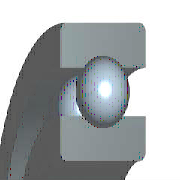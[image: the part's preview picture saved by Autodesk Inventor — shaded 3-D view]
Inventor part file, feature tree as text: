
AUTODESK INVENTOR PART (.ipt)
format: ipt  version: 2021 (Build 250183000, 183)  size: 447,488 bytes
history: native  units: mm (DEFAULTED — no unit token found)
features: sketch x5, other x3, plane x2, pattern_circular x1, fillet x1
ambient origin geometry x8: Origin, YZ Plane, XZ Plane, XY Plane, X Axis, Y Axis, Z Axis, Center Point
bodies: Solid1 (feature_tree)
feature tree (12):
  sketch  "Sketch1"  dims[d2=72.0mm]
  other  "WorkPoint1"
  other  "WorkAxis1"
  plane  "WorkPlane3"
  plane  "WorkPlane4"
  sketch  "Sketch4"  dims[d5=7.0mm]
  other  "WorkPoint2"
  pattern_circular  "PolarArray1"  Count=2  [1 undecoded]
  fillet  "Fillet1"  Radius=25.0mm
  sketch  "Sketch2"  dims[d3=37.0mm]
  sketch  "Sketch3"  dims[d4=19.0mm]
  sketch  "Sketch5"  dims[d6=360.0deg d7=0.0mm d8=15.6mm d9=3.6mm d10=360.0deg d11=-7.0mm d12=0.0mm d13=0.0mm d14=15.6001mm d15=3.6001mm d16=360.0deg d17=133.166667mm d19=360.0deg d20=0.3mm d21=14.42mm d22=15.5mm d23=16.58mm d26=0.0mm d27=0.0mm d28=0.0mm d29=0.0mm d30=0.0mm]
note: 1 required parameter value undecoded (feature->parameter linkage not recoverable at this tier; creation-order binding heuristic only, values carry confidence <= 0.55)
